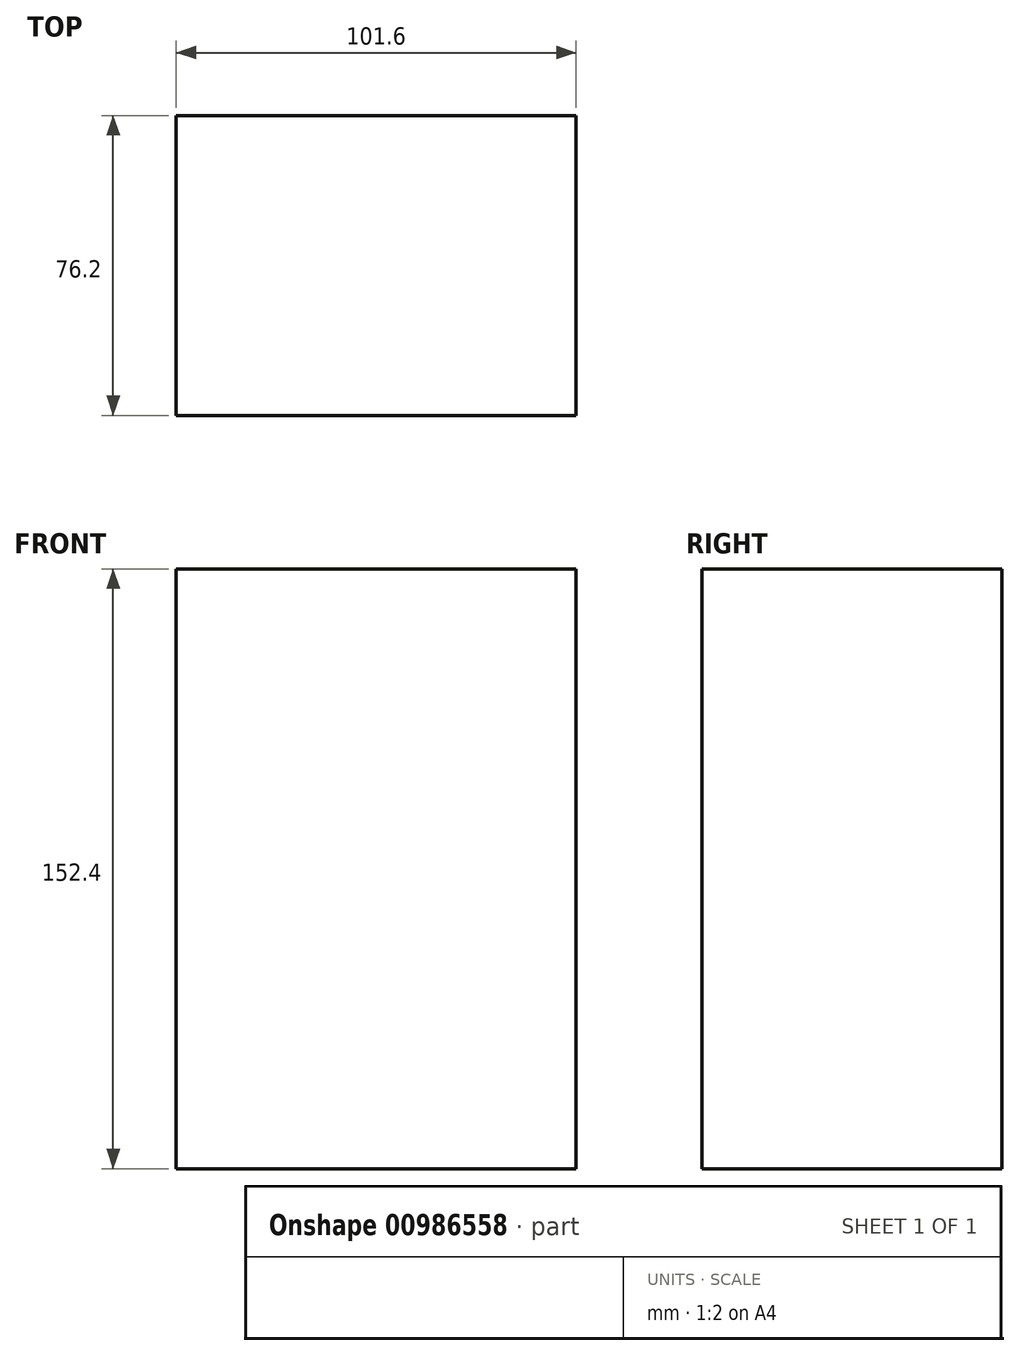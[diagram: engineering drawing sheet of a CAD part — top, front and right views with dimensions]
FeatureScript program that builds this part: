
annotation { "Feature Type Name" : "Feature", "Feature Type Description" : "" }
export const myFeature = defineFeature(function(context is Context, id is Id, definition is map)
    precondition{}
    {
        {
            var Q0;
            Q0=qCreatedBy(makeId("Top.planeOp"),FACE);
            var sketch = newSketch(context, id + "F0", { "sketchPlane" : qUnion([Q0])});
            skLineSegment(sketch, "E0.bottom", {"start": v(-101.6, -76.2) * mm, "end": v(0, -76.2) * mm});
            skLineSegment(sketch, "E0.top", {"start": v(-101.6, 0) * mm, "end": v(0, 0) * mm});
            skLineSegment(sketch, "E0.left", {"start": v(-101.6, -76.2) * mm, "end": v(-101.6, 0) * mm});
            skLineSegment(sketch, "E0.right", {"start": v(0, -76.2) * mm, "end": v(0, 0) * mm});
            skSolve(sketch);
        }
        {
            var Q0;
            Q0=makeQuery(id+"F0.imprint","IMPRINT",FACE,{"disambiguationData":[TD([[makeQuery(id+"F0.imprint","IMPRINT",EDGE,{"derivedFrom":sQuery(id+"F0.wireOp",EDGE,"E0.bottom")}),1.0]])]});
            extrude(context, id + "F1", {"entities" : qUnion([Q0]), "depth" : 152.4 * mm, "offsetDistance" : 25.4 * mm});
        }
    });
